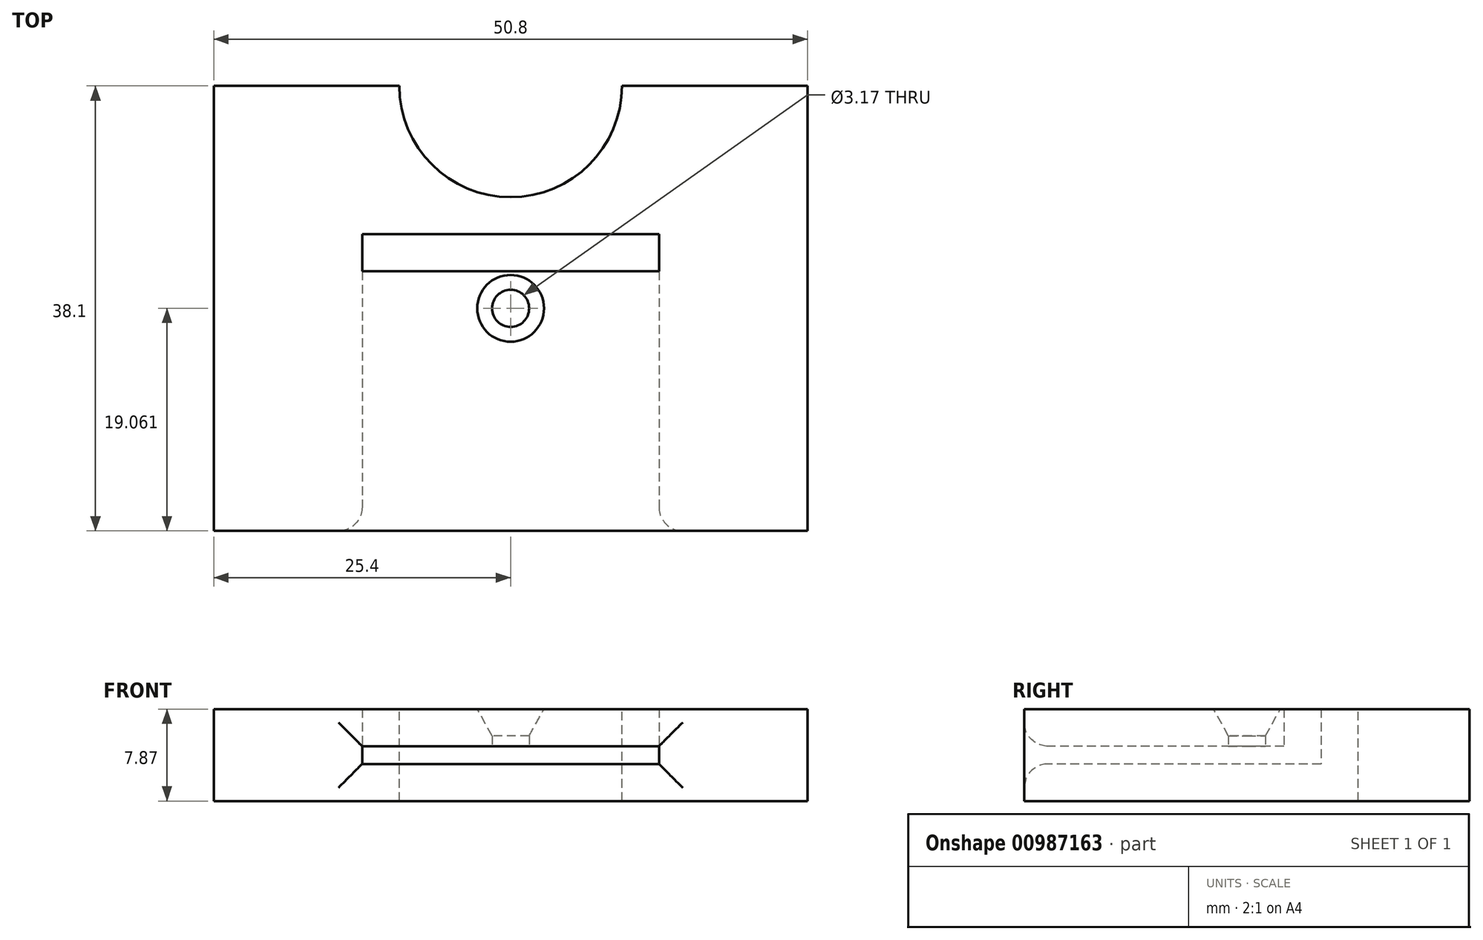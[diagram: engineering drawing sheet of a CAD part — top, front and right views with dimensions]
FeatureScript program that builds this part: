
annotation { "Feature Type Name" : "Feature", "Feature Type Description" : "" }
export const myFeature = defineFeature(function(context is Context, id is Id, definition is map)
    precondition{}
    {
        {
            var Q0;
            Q0=qCreatedBy(makeId("Top.planeOp"),FACE);
            var sketch = newSketch(context, id + "F0", { "sketchPlane" : qUnion([Q0])});
            skLineSegment(sketch, "E0.1", {"start": v(0.28, 40.12) * mm, "end": v(10.19, 40.12) * mm});
            skLineSegment(sketch, "E0.2", {"start": v(-9.63, 40.12) * mm, "end": v(0.28, 40.12) * mm});
            skLineSegment(sketch, "E1", {"start": v(-9.25, 52.82) * mm, "end": v(-25.12, 52.82) * mm});
            skLineSegment(sketch, "E2", {"start": v(-25.12, 52.82) * mm, "end": v(-25.12, 14.72) * mm});
            skLineSegment(sketch, "E3", {"start": v(-25.12, 14.72) * mm, "end": v(25.68, 14.72) * mm});
            skLineSegment(sketch, "E4", {"start": v(25.68, 14.72) * mm, "end": v(25.68, 52.82) * mm});
            skLineSegment(sketch, "E5", {"start": v(25.68, 52.82) * mm, "end": v(9.8, 52.82) * mm});
            skCircle(sketch, "E6", {"center": v(0.28, 33.4) * mm, "radius": 1.59 * mm});
            skLineSegment(sketch, "E7", {"start": v(0.28, 36.96) * mm, "end": v(-9.58, 36.96) * mm});
            skLineSegment(sketch, "E8", {"start": v(-12.42, 36.96) * mm, "end": v(12.98, 36.96) * mm});
            skArc(sketch, "E9", {"start": v(-9.25, 52.82) * mm, "mid": v(0.28, 43.3) * mm, "end": v(9.8, 52.82) * mm});
            skLineSegment(sketch, "E10", {"start": v(0.28, 40.12) * mm, "end": v(-12.42, 40.12) * mm});
            skLineSegment(sketch, "E11", {"start": v(0.28, 40.12) * mm, "end": v(12.98, 40.12) * mm});
            skLineSegment(sketch, "E12", {"start": v(12.98, 40.12) * mm, "end": v(12.98, 14.72) * mm});
            skLineSegment(sketch, "E13", {"start": v(-12.42, 40.12) * mm, "end": v(-12.42, 14.72) * mm});
            skSolve(sketch);
        }
        {
            var Q0;
            Q0=makeQuery(id+"F0.imprint","IMPRINT",FACE,{"disambiguationData":[TD([[makeQuery(id+"F0.imprint","IMPRINT",EDGE,{"derivedFrom":sQuery(id+"F0.wireOp",EDGE,"E0.1")}),1.0]])]});
            var Q1;
            Q1=makeQuery(id+"F0.imprint","IMPRINT",FACE,{"disambiguationData":[TD([[makeQuery(id+"F0.imprint","IMPRINT",EDGE,{"derivedFrom":sQuery(id+"F0.wireOp",EDGE,"E0.1")}),-1.0]])]});
            var Q2;
            Q2=makeQuery(id+"F0.imprint","IMPRINT",FACE,{"disambiguationData":[TD([[makeQuery(id+"F0.imprint","IMPRINT",EDGE,{"derivedFrom":sQuery(id+"F0.wireOp",EDGE,"E6")}),-1.0]])]});
            var Q3;
            Q3=makeQuery(id+"F0.imprint","IMPRINT",FACE,{"disambiguationData":[TD([[makeQuery(id+"F0.imprint","IMPRINT",EDGE,{"derivedFrom":sQuery(id+"F0.wireOp",EDGE,"E6")}),1.0]])]});
            extrude(context, id + "F1", {"entities" : qUnion([Q0, Q1, Q2, Q3]), "oppositeDirection" : true, "depth" : 3.17 * mm, "offsetDistance" : 25.4 * mm});
        }
        {
            var Q0;
            Q0=makeQuery(id+"F0.imprint","IMPRINT",FACE,{"disambiguationData":[TD([[makeQuery(id+"F0.imprint","IMPRINT",EDGE,{"derivedFrom":sQuery(id+"F0.wireOp",EDGE,"E0.1")}),1.0]])]});
            extrude(context, id + "F2", {"entities" : qUnion([Q0]), "operationType" : NewBodyOperationType.ADD, "depth" : 1.52 * mm, "offsetDistance" : 25.4 * mm});
        }
        {
            var Q0;
            Q0=makeQuery(id+"F2.opExtrude","CAP_FACE",FACE,{"disambiguationData":[OSD([sQuery(id+"F0.wireOp",EDGE,"E0.1"),sQuery(id+"F0.wireOp",EDGE,"E0.2"),sQuery(id+"F0.wireOp",EDGE,"E1"),sQuery(id+"F0.wireOp",EDGE,"E2"),sQuery(id+"F0.wireOp",EDGE,"E3"),sQuery(id+"F0.wireOp",EDGE,"E4"),sQuery(id+"F0.wireOp",EDGE,"E5"),sQuery(id+"F0.wireOp",EDGE,"E9"),sQuery(id+"F0.wireOp",EDGE,"E10"),sQuery(id+"F0.wireOp",EDGE,"E11"),sQuery(id+"F0.wireOp",EDGE,"E12"),sQuery(id+"F0.wireOp",EDGE,"E13")])],"isStart":false});
            var sketch = newSketch(context, id + "F3", { "sketchPlane" : qUnion([Q0])});
            skLineSegment(sketch, "E14", {"start": v(-12.42, 14.72) * mm, "end": v(12.98, 14.72) * mm});
            skLineSegment(sketch, "E15", {"start": v(-12.42, 40.12) * mm, "end": v(-12.42, 36.95) * mm});
            skLineSegment(sketch, "E16", {"start": v(-12.42, 36.95) * mm, "end": v(12.98, 36.95) * mm});
            skLineSegment(sketch, "E17", {"start": v(0.28, 40.12) * mm, "end": v(0.28, 33.78) * mm});
            skCircle(sketch, "E18", {"center": v(0.28, 33.78) * mm, "radius": 1.59 * mm});
            skSolve(sketch);
        }
        {
            var Q0;
            {var subQ0=sQuery(id+"F3.wireOp",EDGE,"E15");Q0=makeQuery(id+"F3.imprint","IMPRINT",FACE,{"disambiguationData":[TD([[makeQuery(id+"F3.imprint","IMPRINT",EDGE,{"derivedFrom":subQ0}),-1.0]])]});}
            var Q1;
            {var subQ8=sQuery(id+"F3.wireOp",EDGE,"E14");Q1=makeQuery(id+"F3.imprint","IMPRINT",FACE,{"disambiguationData":[TD([[makeQuery(id+"F3.imprint","IMPRINT",EDGE,{"derivedFrom":subQ8}),1.0]])]});}
            extrude(context, id + "F4", {"entities" : qUnion([Q0, Q1]), "operationType" : NewBodyOperationType.ADD, "depth" : 3.17 * mm, "offsetDistance" : 25.4 * mm});
        }
        {
            var Q0;
            Q0=makeQuery(id+"F4.opExtrude","CAP_EDGE",EDGE,{"disambiguationData":[OSD([sQuery(id+"F0.wireOp",EDGE,"E3"),sQuery(id+"F3.wireOp",EDGE,"E14")])],"isStart":true});
            var Q1;
            Q1=makeQuery(id+"F1.opExtrude","CAP_EDGE",EDGE,{"disambiguationData":[OSD([sQuery(id+"F0.wireOp",EDGE,"E3")])],"isStart":true});
            var Q2;
            Q2=makeQuery(id+"F2.opExtrude","SWEPT_EDGE",EDGE,{"disambiguationData":[OSD([sQuery(id+"F0.wireOp",EDGE,"E3"),sQuery(id+"F0.wireOp",EDGE,"E13")])]});
            var Q3;
            Q3=makeQuery(id+"F2.opExtrude","SWEPT_EDGE",EDGE,{"disambiguationData":[OSD([sQuery(id+"F0.wireOp",EDGE,"E3"),sQuery(id+"F0.wireOp",EDGE,"E12")])]});
            fillet(context, id + "F5", {"entities" : qUnion([Q0, Q1, Q2, Q3]), "radius" : 2.03 * mm, "tangentPropagation" : true, "allowEdgeOverflow" : false});
        }
        {
            var Q0;
            Q0=makeQuery(id+"F4.opExtrude","CAP_EDGE",EDGE,{"disambiguationData":[OSD([sQuery(id+"F3.wireOp",EDGE,"E18")])],"isStart":false});
            chamfer(context, id + "F6", {"entities" : qUnion([Q0]), "chamferType" : ChamferType.TWO_OFFSETS, "width1" : 2.3 * mm, "oppositeDirection" : false, "width2" : 1.27 * mm, "tangentPropagation" : true});
        }
    });
